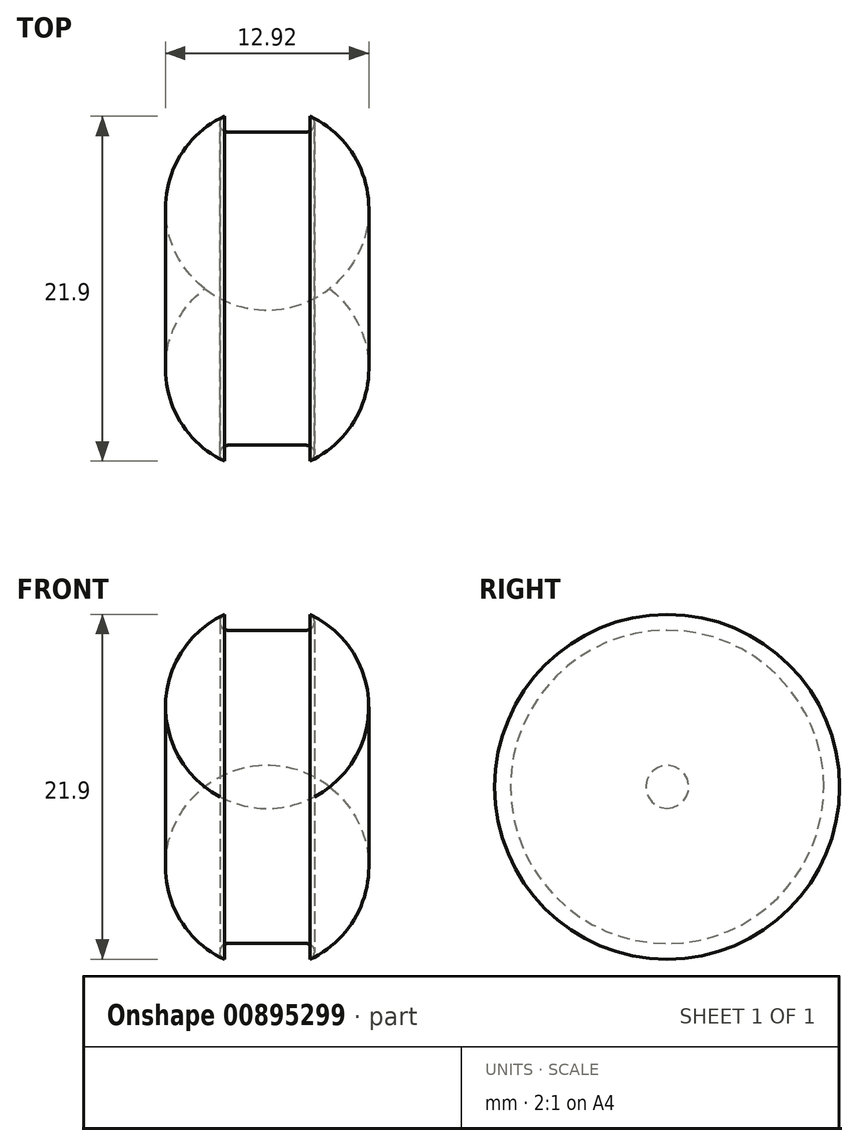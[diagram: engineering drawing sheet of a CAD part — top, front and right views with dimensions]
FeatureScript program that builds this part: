
annotation { "Feature Type Name" : "Feature", "Feature Type Description" : "" }
export const myFeature = defineFeature(function(context is Context, id is Id, definition is map)
    precondition{}
    {
        {
            var Q0;
            Q0=qCreatedBy(makeId("Top.planeOp"),FACE);
            var sketch = newSketch(context, id + "F0", { "sketchPlane" : qUnion([Q0])});
            skLineSegment(sketch, "E0", {"start": v(-2.7, 10.95) * mm, "end": v(-2.7, 10.95) * mm});
            skLineSegment(sketch, "E1", {"start": v(-3, 10.5) * mm, "end": v(-3, 10.45) * mm});
            skLineSegment(sketch, "E2", {"start": v(-2.5, 9.95) * mm, "end": v(-2.5, 9.95) * mm});
            skPoint(sketch, "E3.visualSharp", {"position": v(-3, 9.95) * mm});
            skArc(sketch, "E3.filletArc", {"start": v(-3, 10.45) * mm, "mid": v(-2.85, 10.1) * mm, "end": v(-2.5, 9.95) * mm});
            skPoint(sketch, "E4.visualSharp", {"position": v(-3, 10.82) * mm});
            skArc(sketch, "E4.filletArc", {"start": v(-2.7, 10.95) * mm, "mid": v(-2.92, 10.77) * mm, "end": v(-3, 10.5) * mm});
            skLineSegment(sketch, "E5.MirrorCS", {"start": v(3, 10.5) * mm, "end": v(3, 10.45) * mm});
            skArc(sketch, "E6.MirrorCS", {"start": v(3, 10.45) * mm, "mid": v(2.85, 10.1) * mm, "end": v(2.5, 9.95) * mm});
            skArc(sketch, "E7.MirrorCS", {"start": v(2.7, 10.95) * mm, "mid": v(2.92, 10.77) * mm, "end": v(3, 10.5) * mm});
            skLineSegment(sketch, "E8.MirrorCS", {"start": v(2.7, 10.95) * mm, "end": v(2.7, 10.95) * mm});
            skPoint(sketch, "E9.MirrorP", {"position": v(3, 9.95) * mm});
            skPoint(sketch, "E10.MirrorP", {"position": v(3, 10.82) * mm});
            skLineSegment(sketch, "E11.MirrorCS", {"start": v(2.5, 9.95) * mm, "end": v(2.4, 9.95) * mm});
            skPoint(sketch, "E12.visualSharp", {"position": v(0, 12.2) * mm});
            skArc(sketch, "E12.filletArc", {"start": v(2.7, 10.95) * mm, "mid": v(0, 11.55) * mm, "end": v(-2.7, 10.95) * mm});
            skPoint(sketch, "E13.visualSharp", {"position": v(0, 9.95) * mm});
            skLineSegment(sketch, "E14", {"start": v(0, 0) * mm, "end": v(4.65, 0) * mm, "construction": true});
            skLineSegment(sketch, "E15", {"start": v(3.05, 9.95) * mm, "end": v(4.75, 9.95) * mm, "construction": true});
            skLineSegment(sketch, "E16", {"start": v(-2.5, 9.95) * mm, "end": v(2.5, 9.95) * mm});
            skSolve(sketch);
        }
        {
            var Q0;
            Q0=makeQuery(id+"F0.imprint","IMPRINT",FACE,{"disambiguationData":[TD([[makeQuery(id+"F0.imprint","IMPRINT",EDGE,{"derivedFrom":sQuery(id+"F0.wireOp",EDGE,"E1")}),1.0]])]});
            var Q1;
            Q1=sQuery(id+"F0.wireOp",EDGE,"E14");
            revolve(context, id + "F1", {"surfaceOperationType" : NewSurfaceOperationType.NEW, "entities" : qUnion([Q0]), "axis" : qUnion([Q1]), "revolveType" : RevolveType.FULL});
        }
    });
